# Revit family: Corso 1.0
name_source: partatom
category: Lighting Fixtures
units: mm (PartAtom-declared; Revit-internal decimal feet)

## family parameters
Cut with Voids When Loaded = Yes
Host = Face
Light Source = Yes
Part Type = Normal
Room Calculation Point = Yes
Round Connector Dimension = Use Diameter
Shared = No

## types (5) — shared parameters
Apparent Load = 0 VA
Apparent Load Phase 1 = 4 W
Body = L&L_Technopolymer
CRI = 80
Code = -
Color Filter = 16777215
Control system = ON/OFF
Cutout dimensions = -
Default Elevation = 1219 mm
Delivered lumen output = 178 lm (3000K, 13°)
Description = recessed for outdoor applications
Dimming Lamp Color Temperature Shift = <None>
Emit from Line Length = 610 mm
Energy efficiency class = A A+ A++
Features = Speedy installation: electrical wiring simplified by the ability to connect the electrical cables directly to the fixture
Height Void = 100 mm  [stored 0.328084 ft]
Height mm = 108 mm  [stored 0.354331 ft]
IP = IP65, IP67
LED Colour = 2700K, 3000K, 4000K
Length mm = 85 mm  [stored 0.278871 ft]
Lens = L&L_Tempered extra-clear glass
Lumen output at source = 224 lm (3000K)
Manufacturer = L&L Luce&Light
Material = body in thermally conductive plastic, trim in AISI 316L stainless steel, screen in tempered, transparent extra-clear glass
Model = Corso 1.0
Mounting = recessed (floor)
No. and type of led = 1 power LED, 1/4 ANSI BIN, 50 000h L90 B10 (Ta 25°C)
Notes = -
Power = 3.5W
Power Supply = L&L_Technopolymer
Power cables = -
Power supply = 110-230Vac
Power supply unit = built-in
Radius Void = 40 mm
Tilt Angle = 90.00°
Tiltable = -
Trim = L&L_Steel inox AISI 316L
URL = https://www.lucelight.it
URL Accessories and power supply units = https://www.lucelight.it
URL Catalogue = https://www.lucelight.it
URL DXF = https://www.lucelight.it
URL Description = https://www.lucelight.it
URL General code = https://www.lucelight.it
URL IES Photometric file = https://www.lucelight.it
URL Image = https://www.lucelight.it
Voltage = 230 V
Weight kg = 0.40 kg
Width mm = 85 mm  [stored 0.278871 ft]
Wiring = -

## per-type parameters (varying)
| type | Optics | Photometric Web File |
| Corso 1.0 W 12°x45° (3000K 3.5W 110-230Vac) | 12°x45° | CORSO 1.0 W 12°x45° [3000K 3.5W 110-230Vac].IES |
| Corso 1.0 S 13° (3000K 3.5W 110-230Vac) | 13° | CORSO 1.0 S 13° [3000K 3.5W 110-230Vac].IES |
| Corso 1.0 M 28° (3000K 3.5W 110-230Vac) | 28° | CORSO 1.0 M 28° [3000K 3.5W 110-230Vac].IES |
| Corso 1.0 L 37° (3000K 3.5W 110-230Vac) | 37° | CORSO 1.0 L 37° [3000K 3.5W 110-230Vac].IES |
| Corso 1.0 diffuse (3000K 3.5W 110-230Vac) | diffuse | CORSO 1.0 D [3000K 3.5W 110-230Vac].IES |

note: [stored X ft] marks values corroborated as IEEE doubles in the binary element streams (Revit-internal decimal feet)

## geometry (parser evidence)
native form markers: Blend x2, Sweep x4
no freeform markers — native parametric forms only
